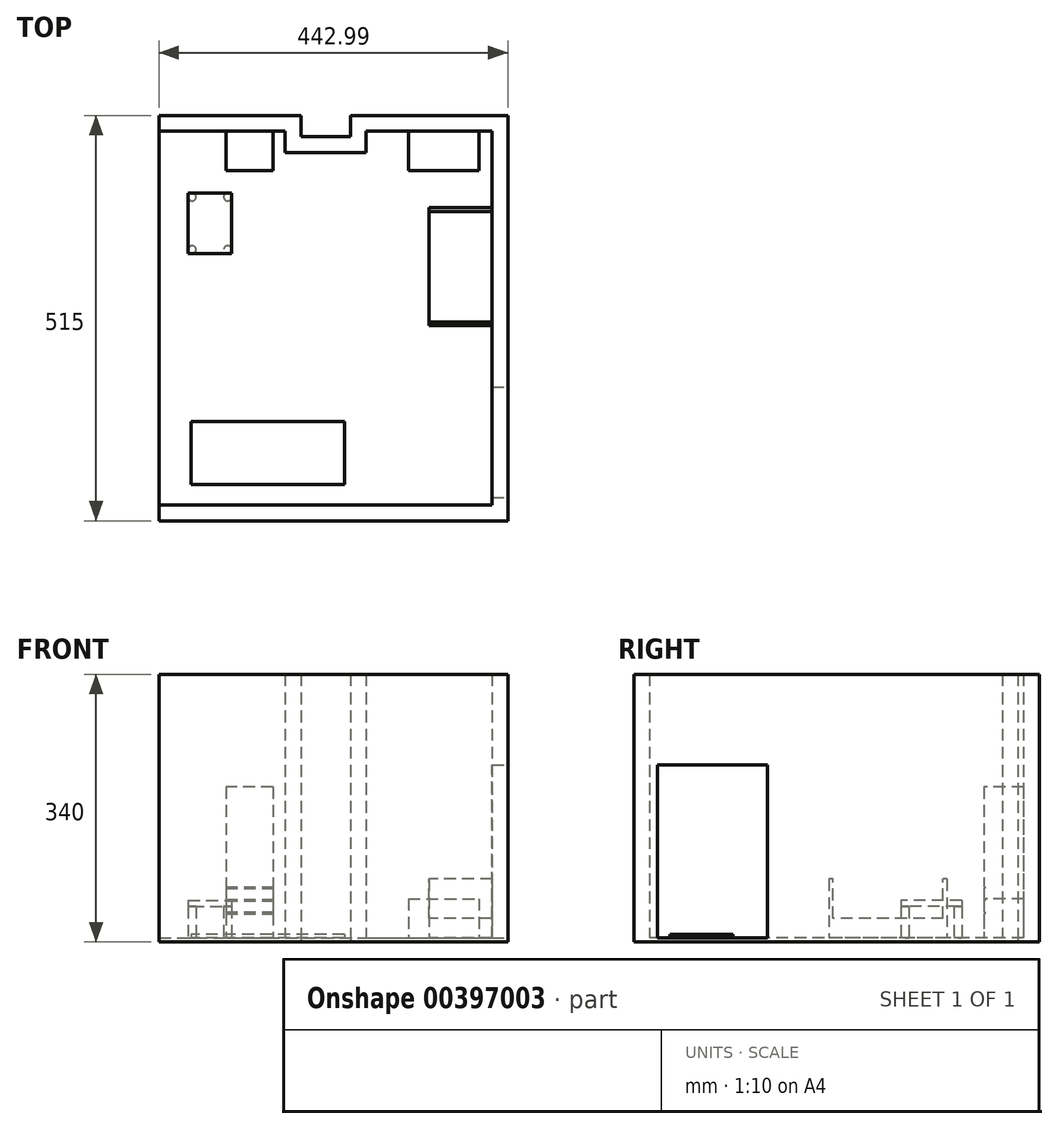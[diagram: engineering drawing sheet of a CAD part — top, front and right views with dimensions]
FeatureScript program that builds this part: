
annotation { "Feature Type Name" : "Feature", "Feature Type Description" : "" }
export const myFeature = defineFeature(function(context is Context, id is Id, definition is map)
    precondition{}
    {
        {
            var Q0;
            Q0=qCreatedBy(makeId("Top.planeOp"),FACE);
            var sketch = newSketch(context, id + "F0", { "sketchPlane" : qUnion([Q0])});
            skLineSegment(sketch, "E0.bottom", {"start": v(-209.62, 330.23) * mm, "end": v(-49.62, 330.23) * mm});
            skLineSegment(sketch, "E0.top", {"start": v(-209.62, -144.77) * mm, "end": v(213.38, -144.77) * mm});
            skLineSegment(sketch, "E0.right", {"start": v(213.38, 330.23) * mm, "end": v(213.38, -144.77) * mm});
            skLineSegment(sketch, "E1.top", {"start": v(-49.62, 303.23) * mm, "end": v(53.38, 303.23) * mm});
            skLineSegment(sketch, "E1.left", {"start": v(-49.62, 330.23) * mm, "end": v(-49.62, 303.23) * mm});
            skLineSegment(sketch, "E1.right", {"start": v(53.38, 330.23) * mm, "end": v(53.38, 303.23) * mm});
            skLineSegment(sketch, "E2", {"start": v(53.38, 330.23) * mm, "end": v(213.38, 330.23) * mm});
            skLineSegment(sketch, "E3.0", {"start": v(-209.62, -164.77) * mm, "end": v(233.37, -164.77) * mm});
            skLineSegment(sketch, "E3.1", {"start": v(233.37, 350.23) * mm, "end": v(233.37, -164.77) * mm});
            skLineSegment(sketch, "E3.2", {"start": v(33.38, 350.23) * mm, "end": v(233.37, 350.23) * mm});
            skLineSegment(sketch, "E3.3", {"start": v(-209.62, 350.23) * mm, "end": v(-29.63, 350.23) * mm});
            skLineSegment(sketch, "E3.4", {"start": v(-29.63, 350.23) * mm, "end": v(-29.63, 323.23) * mm});
            skLineSegment(sketch, "E3.5", {"start": v(-29.63, 323.23) * mm, "end": v(33.38, 323.23) * mm});
            skLineSegment(sketch, "E3.6", {"start": v(33.38, 350.23) * mm, "end": v(33.38, 323.23) * mm});
            skLineSegment(sketch, "E4", {"start": v(-209.62, 330.23) * mm, "end": v(-209.62, 350.23) * mm});
            skLineSegment(sketch, "E5", {"start": v(-209.62, -164.77) * mm, "end": v(-209.62, -144.77) * mm});
            skLineSegment(sketch, "E6", {"start": v(-209.62, 330.23) * mm, "end": v(-209.62, -144.77) * mm});
            skSolve(sketch);
        }
        {
            var Q0;
            Q0=makeQuery(id+"F0.imprint","IMPRINT",FACE,{"disambiguationData":[TD([[makeQuery(id+"F0.imprint","IMPRINT",EDGE,{"derivedFrom":sQuery(id+"F0.wireOp",EDGE,"E0.bottom")}),1.0]])]});
            extrude(context, id + "F1", {"entities" : qUnion([Q0]), "depth" : 340 * mm});
        }
        {
            var Q0;
            Q0=makeQuery(id+"F0.imprint","IMPRINT",FACE,{"disambiguationData":[TD([[makeQuery(id+"F0.imprint","IMPRINT",EDGE,{"derivedFrom":sQuery(id+"F0.wireOp",EDGE,"E0.bottom")}),-1.0]])]});
            extrude(context, id + "F2", {"entities" : qUnion([Q0]), "operationType" : NewBodyOperationType.ADD, "depth" : 5 * mm});
        }
        {
            var Q0;
            Q0=makeQuery(id+"F1.opExtrude","SWEPT_FACE",FACE,{"disambiguationData":[OSD([sQuery(id+"F0.wireOp",EDGE,"E3.1")])]});
            var sketch = newSketch(context, id + "F3", { "sketchPlane" : qUnion([Q0])});
            skLineSegment(sketch, "E7.top", {"start": v(-134.77, 225) * mm, "end": v(5.23, 225) * mm});
            skLineSegment(sketch, "E8", {"start": v(-134.77, 225) * mm, "end": v(-134.77, 5) * mm});
            skLineSegment(sketch, "E9", {"start": v(-134.77, 5) * mm, "end": v(5.23, 5) * mm});
            skLineSegment(sketch, "E10", {"start": v(5.23, 5) * mm, "end": v(5.23, 225) * mm});
            skSolve(sketch);
        }
        {
            var Q0;
            Q0=makeQuery(id+"F3.imprint","IMPRINT",FACE,{"disambiguationData":[TD([[makeQuery(id+"F3.imprint","IMPRINT",EDGE,{"derivedFrom":sQuery(id+"F3.wireOp",EDGE,"E7.top")}),-1.0]])]});
            extrude(context, id + "F4", {"entities" : qUnion([Q0]), "operationType" : NewBodyOperationType.REMOVE, "oppositeDirection" : true, "depth" : 20 * mm});
        }
        {
            var Q0;
            Q0=makeQuery(id+"F4.boolean.opBoolean","MERGE",FACE,{"derivedFrom":[makeQuery(id+"F2.opExtrude","CAP_FACE",FACE,{"disambiguationData":[OSD([sQuery(id+"F0.wireOp",EDGE,"E0.bottom"),sQuery(id+"F0.wireOp",EDGE,"E0.top"),sQuery(id+"F0.wireOp",EDGE,"E0.right"),sQuery(id+"F0.wireOp",EDGE,"E1.top"),sQuery(id+"F0.wireOp",EDGE,"E1.left"),sQuery(id+"F0.wireOp",EDGE,"E1.right"),sQuery(id+"F0.wireOp",EDGE,"E2"),sQuery(id+"F0.wireOp",EDGE,"E6")])],"isStart":false}),makeQuery(id+"F4.opExtrude","SWEPT_FACE",FACE,{"disambiguationData":[OSD([sQuery(id+"F3.wireOp",EDGE,"E9")])]})]});
            var sketch = newSketch(context, id + "F5", { "sketchPlane" : qUnion([Q0])});
            skLineSegment(sketch, "E11.bottom", {"start": v(213.38, 233.13) * mm, "end": v(133.38, 233.13) * mm});
            skLineSegment(sketch, "E11.top", {"start": v(213.38, 83.13) * mm, "end": v(133.38, 83.13) * mm});
            skLineSegment(sketch, "E11.left", {"start": v(213.38, 233.13) * mm, "end": v(213.38, 83.13) * mm});
            skLineSegment(sketch, "E11.right", {"start": v(133.38, 233.13) * mm, "end": v(133.38, 83.13) * mm});
            skSolve(sketch);
        }
        {
            var Q0;
            Q0=makeQuery(id+"F5.imprint","IMPRINT",FACE,{"disambiguationData":[TD([[makeQuery(id+"F5.imprint","IMPRINT",EDGE,{"derivedFrom":sQuery(id+"F5.wireOp",EDGE,"E11.bottom")}),1.0]])]});
            extrude(context, id + "F6", {"entities" : qUnion([Q0]), "depth" : 75 * mm});
        }
        {
            var Q0;
            Q0=makeQuery(id+"F6.opExtrude","CAP_FACE",FACE,{"disambiguationData":[OSD([sQuery(id+"F5.wireOp",EDGE,"E11.bottom"),sQuery(id+"F5.wireOp",EDGE,"E11.top"),sQuery(id+"F5.wireOp",EDGE,"E11.left"),sQuery(id+"F5.wireOp",EDGE,"E11.right")])],"isStart":false});
            var sketch = newSketch(context, id + "F7", { "sketchPlane" : qUnion([Q0])});
            skLineSegment(sketch, "E12.bottom", {"start": v(213.38, 228.13) * mm, "end": v(133.38, 228.13) * mm});
            skLineSegment(sketch, "E12.top", {"start": v(213.38, 88.13) * mm, "end": v(133.38, 88.13) * mm});
            skLineSegment(sketch, "E12.left", {"start": v(213.38, 228.13) * mm, "end": v(213.38, 88.13) * mm});
            skLineSegment(sketch, "E12.right", {"start": v(133.38, 228.13) * mm, "end": v(133.38, 88.13) * mm});
            skSolve(sketch);
        }
        {
            var Q0;
            Q0=makeQuery(id+"F7.imprint","IMPRINT",FACE,{"disambiguationData":[TD([[makeQuery(id+"F7.imprint","IMPRINT",EDGE,{"derivedFrom":sQuery(id+"F7.wireOp",EDGE,"E12.bottom")}),1.0]])]});
            extrude(context, id + "F8", {"entities" : qUnion([Q0]), "operationType" : NewBodyOperationType.REMOVE, "oppositeDirection" : true, "depth" : 50 * mm});
        }
        {
            var Q0;
            Q0=makeQuery(id+"F4.boolean.opBoolean","MERGE",FACE,{"derivedFrom":[makeQuery(id+"F2.opExtrude","CAP_FACE",FACE,{"disambiguationData":[OSD([sQuery(id+"F0.wireOp",EDGE,"E0.bottom"),sQuery(id+"F0.wireOp",EDGE,"E0.top"),sQuery(id+"F0.wireOp",EDGE,"E0.right"),sQuery(id+"F0.wireOp",EDGE,"E1.top"),sQuery(id+"F0.wireOp",EDGE,"E1.left"),sQuery(id+"F0.wireOp",EDGE,"E1.right"),sQuery(id+"F0.wireOp",EDGE,"E2"),sQuery(id+"F0.wireOp",EDGE,"E6")])],"isStart":false}),makeQuery(id+"F4.opExtrude","SWEPT_FACE",FACE,{"disambiguationData":[OSD([sQuery(id+"F3.wireOp",EDGE,"E9")])]})]});
            var sketch = newSketch(context, id + "F9", { "sketchPlane" : qUnion([Q0])});
            skLineSegment(sketch, "E13.bottom", {"start": v(196.92, 330.23) * mm, "end": v(106.92, 330.23) * mm});
            skLineSegment(sketch, "E13.top", {"start": v(196.92, 280.23) * mm, "end": v(106.92, 280.23) * mm});
            skLineSegment(sketch, "E13.left", {"start": v(196.92, 330.23) * mm, "end": v(196.92, 280.23) * mm});
            skLineSegment(sketch, "E13.right", {"start": v(106.92, 330.23) * mm, "end": v(106.92, 280.23) * mm});
            skSolve(sketch);
        }
        {
            var Q0;
            Q0=makeQuery(id+"F9.imprint","IMPRINT",FACE,{"disambiguationData":[TD([[makeQuery(id+"F9.imprint","IMPRINT",EDGE,{"derivedFrom":sQuery(id+"F9.wireOp",EDGE,"E13.bottom")}),-1.0]])]});
            extrude(context, id + "F10", {"entities" : qUnion([Q0]), "depth" : 50 * mm});
        }
        {
            var Q0;
            Q0=makeQuery(id+"F4.boolean.opBoolean","MERGE",FACE,{"derivedFrom":[makeQuery(id+"F2.opExtrude","CAP_FACE",FACE,{"disambiguationData":[OSD([sQuery(id+"F0.wireOp",EDGE,"E0.bottom"),sQuery(id+"F0.wireOp",EDGE,"E0.top"),sQuery(id+"F0.wireOp",EDGE,"E0.right"),sQuery(id+"F0.wireOp",EDGE,"E1.top"),sQuery(id+"F0.wireOp",EDGE,"E1.left"),sQuery(id+"F0.wireOp",EDGE,"E1.right"),sQuery(id+"F0.wireOp",EDGE,"E2"),sQuery(id+"F0.wireOp",EDGE,"E6")])],"isStart":false}),makeQuery(id+"F4.opExtrude","SWEPT_FACE",FACE,{"disambiguationData":[OSD([sQuery(id+"F3.wireOp",EDGE,"E9")])]})]});
            var sketch = newSketch(context, id + "F11", { "sketchPlane" : qUnion([Q0])});
            skLineSegment(sketch, "E14.bottom", {"start": v(-64.84, 330.23) * mm, "end": v(-124.84, 330.23) * mm});
            skLineSegment(sketch, "E14.top", {"start": v(-64.84, 280.23) * mm, "end": v(-124.84, 280.23) * mm});
            skLineSegment(sketch, "E14.left", {"start": v(-64.84, 330.23) * mm, "end": v(-64.84, 280.23) * mm});
            skLineSegment(sketch, "E14.right", {"start": v(-124.84, 330.23) * mm, "end": v(-124.84, 280.23) * mm});
            skSolve(sketch);
        }
        {
            var Q0;
            Q0=makeQuery(id+"F11.imprint","IMPRINT",FACE,{"disambiguationData":[TD([[makeQuery(id+"F11.imprint","IMPRINT",EDGE,{"derivedFrom":sQuery(id+"F11.wireOp",EDGE,"E14.bottom")}),-1.0]])]});
            extrude(context, id + "F12", {"entities" : qUnion([Q0]), "depth" : 192 * mm});
        }
        {
            var Q0;
            Q0=makeQuery(id+"F12.opExtrude","SWEPT_FACE",FACE,{"disambiguationData":[OSD([sQuery(id+"F11.wireOp",EDGE,"E14.top")])]});
            var sketch = newSketch(context, id + "F13", { "sketchPlane" : qUnion([Q0])});
            skLineSegment(sketch, "E15.bottom", {"start": v(-124.84, 38) * mm, "end": v(-64.84, 38) * mm});
            skLineSegment(sketch, "E15.top", {"start": v(-124.84, 36) * mm, "end": v(-64.84, 36) * mm});
            skLineSegment(sketch, "E15.left", {"start": v(-124.84, 38) * mm, "end": v(-124.84, 36) * mm});
            skLineSegment(sketch, "E15.right", {"start": v(-64.84, 38) * mm, "end": v(-64.84, 36) * mm});
            skLineSegment(sketch, "E16.bottom", {"start": v(-124.84, 54) * mm, "end": v(-64.84, 54) * mm});
            skLineSegment(sketch, "E16.top", {"start": v(-124.84, 52) * mm, "end": v(-64.84, 52) * mm});
            skLineSegment(sketch, "E16.left", {"start": v(-124.84, 54) * mm, "end": v(-124.84, 52) * mm});
            skLineSegment(sketch, "E16.right", {"start": v(-64.84, 54) * mm, "end": v(-64.84, 52) * mm});
            skLineSegment(sketch, "E17.bottom", {"start": v(-124.84, 70) * mm, "end": v(-64.84, 70) * mm});
            skLineSegment(sketch, "E17.top", {"start": v(-124.84, 68) * mm, "end": v(-64.84, 68) * mm});
            skLineSegment(sketch, "E17.left", {"start": v(-124.84, 70) * mm, "end": v(-124.84, 68) * mm});
            skLineSegment(sketch, "E17.right", {"start": v(-64.84, 70) * mm, "end": v(-64.84, 68) * mm});
            skLineSegment(sketch, "E18.bottom", {"start": v(-95.84, 70) * mm, "end": v(-93.84, 70) * mm});
            skLineSegment(sketch, "E18.top", {"start": v(-95.84, 197) * mm, "end": v(-93.84, 197) * mm});
            skLineSegment(sketch, "E18.left", {"start": v(-95.84, 70) * mm, "end": v(-95.84, 197) * mm});
            skLineSegment(sketch, "E18.right", {"start": v(-93.84, 70) * mm, "end": v(-93.84, 197) * mm});
            skSolve(sketch);
        }
        {
            var Q0;
            Q0=makeQuery(id+"F13.imprint","IMPRINT",FACE,{"disambiguationData":[TD([[makeQuery(id+"F13.imprint","IMPRINT",EDGE,{"derivedFrom":sQuery(id+"F13.wireOp",EDGE,"E18.bottom")}),1.0]])]});
            var Q1;
            Q1=makeQuery(id+"F13.imprint","IMPRINT",FACE,{"disambiguationData":[TD([[makeQuery(id+"F13.imprint","IMPRINT",EDGE,{"derivedFrom":sQuery(id+"F13.wireOp",EDGE,"E17.top")}),1.0]])]});
            var Q2;
            Q2=makeQuery(id+"F13.imprint","IMPRINT",FACE,{"disambiguationData":[TD([[makeQuery(id+"F13.imprint","IMPRINT",EDGE,{"derivedFrom":sQuery(id+"F13.wireOp",EDGE,"E16.bottom")}),-1.0]])]});
            var Q3;
            Q3=makeQuery(id+"F13.imprint","IMPRINT",FACE,{"disambiguationData":[TD([[makeQuery(id+"F13.imprint","IMPRINT",EDGE,{"derivedFrom":sQuery(id+"F13.wireOp",EDGE,"E15.bottom")}),-1.0]])]});
            extrude(context, id + "F14", {"entities" : qUnion([Q0, Q1, Q2, Q3]), "operationType" : NewBodyOperationType.REMOVE, "oppositeDirection" : true, "depth" : 1 * mm});
        }
        {
            var Q0;
            Q0=makeQuery(id+"F4.boolean.opBoolean","MERGE",FACE,{"derivedFrom":[makeQuery(id+"F2.opExtrude","CAP_FACE",FACE,{"disambiguationData":[OSD([sQuery(id+"F0.wireOp",EDGE,"E0.bottom"),sQuery(id+"F0.wireOp",EDGE,"E0.top"),sQuery(id+"F0.wireOp",EDGE,"E0.right"),sQuery(id+"F0.wireOp",EDGE,"E1.top"),sQuery(id+"F0.wireOp",EDGE,"E1.left"),sQuery(id+"F0.wireOp",EDGE,"E1.right"),sQuery(id+"F0.wireOp",EDGE,"E2"),sQuery(id+"F0.wireOp",EDGE,"E6")])],"isStart":false}),makeQuery(id+"F4.opExtrude","SWEPT_FACE",FACE,{"disambiguationData":[OSD([sQuery(id+"F3.wireOp",EDGE,"E9")])]})]});
            var sketch = newSketch(context, id + "F15", { "sketchPlane" : qUnion([Q0])});
            skLineSegment(sketch, "E19.bottom", {"start": v(25.74, -38.56) * mm, "end": v(-169.26, -38.56) * mm});
            skLineSegment(sketch, "E19.top", {"start": v(25.74, -118.56) * mm, "end": v(-169.26, -118.56) * mm});
            skLineSegment(sketch, "E19.left", {"start": v(25.74, -38.56) * mm, "end": v(25.74, -118.56) * mm});
            skLineSegment(sketch, "E19.right", {"start": v(-169.26, -38.56) * mm, "end": v(-169.26, -118.56) * mm});
            skSolve(sketch);
        }
        {
            var Q0;
            Q0=makeQuery(id+"F15.imprint","IMPRINT",FACE,{"disambiguationData":[TD([[makeQuery(id+"F15.imprint","IMPRINT",EDGE,{"derivedFrom":sQuery(id+"F15.wireOp",EDGE,"E19.bottom")}),1.0]])]});
            extrude(context, id + "F16", {"entities" : qUnion([Q0]), "depth" : 5 * mm});
        }
        {
            var Q0;
            Q0=makeQuery(id+"F4.boolean.opBoolean","MERGE",FACE,{"derivedFrom":[makeQuery(id+"F2.opExtrude","CAP_FACE",FACE,{"disambiguationData":[OSD([sQuery(id+"F0.wireOp",EDGE,"E0.bottom"),sQuery(id+"F0.wireOp",EDGE,"E0.top"),sQuery(id+"F0.wireOp",EDGE,"E0.right"),sQuery(id+"F0.wireOp",EDGE,"E1.top"),sQuery(id+"F0.wireOp",EDGE,"E1.left"),sQuery(id+"F0.wireOp",EDGE,"E1.right"),sQuery(id+"F0.wireOp",EDGE,"E2"),sQuery(id+"F0.wireOp",EDGE,"E6")])],"isStart":false}),makeQuery(id+"F4.opExtrude","SWEPT_FACE",FACE,{"disambiguationData":[OSD([sQuery(id+"F3.wireOp",EDGE,"E9")])]})]});
            var sketch = newSketch(context, id + "F17", { "sketchPlane" : qUnion([Q0])});
            skCircle(sketch, "E20", {"center": v(-167.65, 246.71) * mm, "radius": 5 * mm});
            skCircle(sketch, "E21.0.1.0", {"center": v(-167.65, 179.71) * mm, "radius": 5 * mm});
            skCircle(sketch, "E21.1.0.0", {"center": v(-122.65, 246.71) * mm, "radius": 5 * mm});
            skCircle(sketch, "E21.1.1.0", {"center": v(-122.65, 179.71) * mm, "radius": 5 * mm});
            skLineSegment(sketch, "E21.direction1", {"start": v(-167.65, 246.71) * mm, "end": v(-122.65, 246.71) * mm, "construction": true});
            skLineSegment(sketch, "E21.direction2", {"start": v(-167.65, 246.71) * mm, "end": v(-167.65, 179.71) * mm, "construction": true});
            skSolve(sketch);
        }
        {
            var Q0;
            Q0=makeQuery(id+"F17.imprint","IMPRINT",FACE,{"disambiguationData":[TD([[makeQuery(id+"F17.imprint","IMPRINT",EDGE,{"derivedFrom":sQuery(id+"F17.wireOp",EDGE,"E20")}),1.0]])]});
            var Q1;
            Q1=makeQuery(id+"F17.imprint","IMPRINT",FACE,{"disambiguationData":[TD([[makeQuery(id+"F17.imprint","IMPRINT",EDGE,{"derivedFrom":sQuery(id+"F17.wireOp",EDGE,"E21.0.1.0")}),1.0]])]});
            var Q2;
            Q2=makeQuery(id+"F17.imprint","IMPRINT",FACE,{"disambiguationData":[TD([[makeQuery(id+"F17.imprint","IMPRINT",EDGE,{"derivedFrom":sQuery(id+"F17.wireOp",EDGE,"E21.1.0.0")}),1.0]])]});
            var Q3;
            Q3=makeQuery(id+"F17.imprint","IMPRINT",FACE,{"disambiguationData":[TD([[makeQuery(id+"F17.imprint","IMPRINT",EDGE,{"derivedFrom":sQuery(id+"F17.wireOp",EDGE,"E21.1.1.0")}),1.0]])]});
            extrude(context, id + "F18", {"entities" : qUnion([Q0, Q1, Q2, Q3]), "depth" : 40 * mm});
        }
        {
            var Q0;
            Q0=makeQuery(id+"F18.opExtrude","CAP_FACE",FACE,{"disambiguationData":[OSD([sQuery(id+"F17.wireOp",EDGE,"E21.0.1.0")])],"isStart":false});
            var sketch = newSketch(context, id + "F19", { "sketchPlane" : qUnion([Q0])});
            skLineSegment(sketch, "E22.bottom", {"start": v(-172.65, 251.71) * mm, "end": v(-117.65, 251.71) * mm});
            skLineSegment(sketch, "E22.top", {"start": v(-172.65, 174.71) * mm, "end": v(-117.65, 174.71) * mm});
            skLineSegment(sketch, "E22.left", {"start": v(-172.65, 251.71) * mm, "end": v(-172.65, 174.71) * mm});
            skLineSegment(sketch, "E22.right", {"start": v(-117.65, 251.71) * mm, "end": v(-117.65, 174.71) * mm});
            skSolve(sketch);
        }
        {
            var Q0;
            Q0 = qSketchRegion(id + "F19", true);
            extrude(context, id + "F20", {"entities" : qUnion([Q0]), "operationType" : NewBodyOperationType.ADD, "depth" : 8 * mm});
        }
    });
